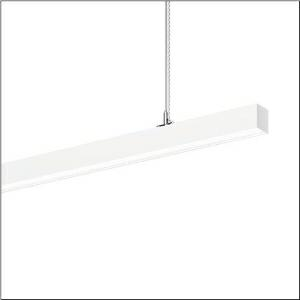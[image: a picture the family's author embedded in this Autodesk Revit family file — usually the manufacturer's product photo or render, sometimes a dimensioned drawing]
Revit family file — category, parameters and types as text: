
# Revit family: silica_21_51mx33tctdw
name_source: partatom
category: Lighting Fixtures
units: mm (PartAtom-declared; Revit-internal decimal feet)

## family parameters
Cut with Voids When Loaded = No
Host = Face
Light Source = No
Part Type = Normal
Room Calculation Point = No
Round Connector Dimension = Use Diameter
Shared = No

## types (1)
- --- (1 x LED, 14340 lm, 134.7 W, 6500K)
    Apparent Load = 135 VA
    CIE Flux Codes = 78 96 99 56 100
    Color Rendering = 80
    Color Temperature = 6500K
    Default Elevation = 1800 mm
    Description = Silica 21, office luminaire, primary optical cover: prismatic diffuser, of PMMA, CAT 2 (L<= 3000cd/m²), light emission: direct/indirect distribution, primary light characteristic: symmetric, installation type: suspended mounting, LED, rated luminous flux: 14.340lm, luminous efficacy: 101lm/W, light colour: 8tw, colour temperature: 2700..6500K, control gear: DALI DT8, with terminal, 3+2-pole, max. 2.5mm², mains connection: 220..240V, AC, 50/60Hz, rated input power: 141.4W, luminaire housing, of aluminium, traffic white (RAL 9016), length: 3.004mm, width: 53mm, height: 53mm, protection rating (complete): IP20, insulation class (complete): insulation class I (protective earthing), certification: CE, permissible operating ambient temperature: 0..+35°C, standard: EN 50419, packaging unit: 1 piece
    Height = 53 mm
    Lamp = 1 x LED
    Lamp Light Flux = 14340 lm
    Lamp Power = 134.7 W
    Lamp count = 1
    Length = 3004 mm
    Luminous efficacy = 106 lm/W
    Manufacturer = Siteco
    ModVariant = No
    Model = 51MX33TCTDW
    Mounting Place = Ceiling
    Mounting Type = Pendant
    Number of Poles = 1
    OnlyDefault = Yes
    Power Factor = 1
    Product Name = Silica 21
    Product group = office luminaire | ceiling pendant
    ProductGroupID = 903
    Protection Class = Protection class I
    Protection Degree = IP 20
    RLX_Detail_Level = 1
    RLX_Emergency_Light_Flux = 0 lm
    RLX_Emergency_Type = 0
    RLX_Emergency_Type_DB = No
    RlxData = <blob elided: 18057 chars, md5=a6b36715>
    Socket = socket
    Standby Power = 0 W
    System Light Flux = 14340 lm
    System Power = 135 W
    Type Comments = individual setting
    Type Image = l_1349007.jpg
    URL = http://relux.com
    VarID = @adj_139265
    Voltage = 0 V
    Weight = 0.00 kg
    Width = 53 mm

## geometry (parser evidence)
native form markers: Blend x4, Sweep x14
no freeform markers — native parametric forms only
